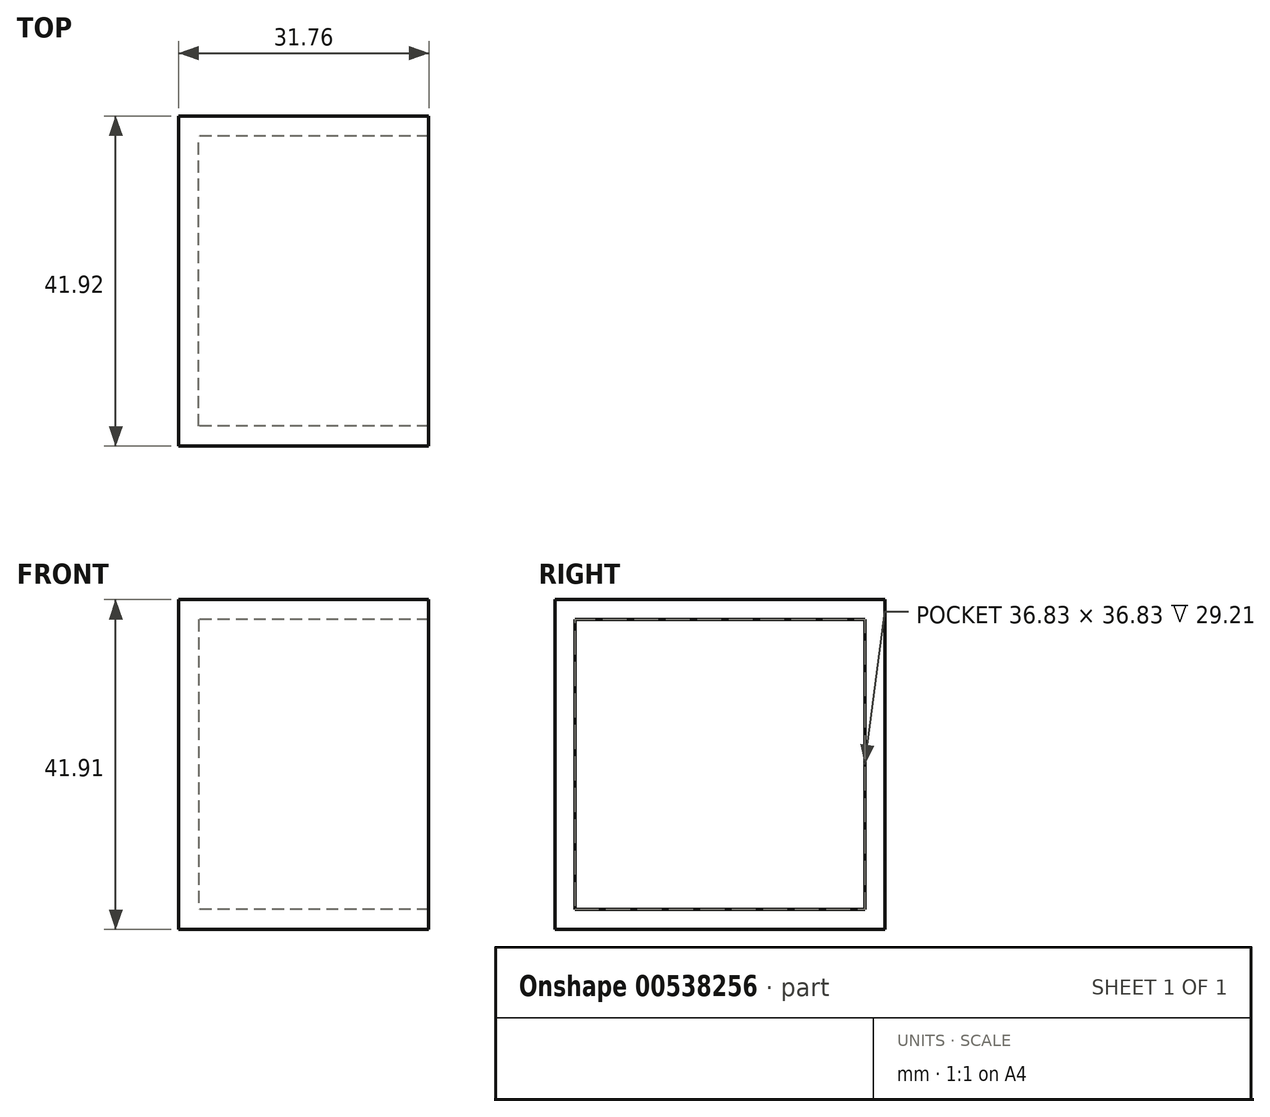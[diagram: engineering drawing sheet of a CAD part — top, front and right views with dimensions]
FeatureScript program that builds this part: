
annotation { "Feature Type Name" : "Feature", "Feature Type Description" : "" }
export const myFeature = defineFeature(function(context is Context, id is Id, definition is map)
    precondition{}
    {
        {
            var Q0;
            Q0=qCreatedBy(makeId("Top.planeOp"),FACE);
            var sketch = newSketch(context, id + "F0", { "sketchPlane" : qUnion([Q0])});
            skPoint(sketch, "E0.middle", {"position": v(0, 0) * mm});
            skLineSegment(sketch, "E1.bottom", {"start": v(14.6, -20.95) * mm, "end": v(-14.6, -20.96) * mm});
            skLineSegment(sketch, "E1.top", {"start": v(14.6, 20.96) * mm, "end": v(-14.6, 20.95) * mm});
            skLineSegment(sketch, "E2.bottom", {"start": v(15.88, -20.96) * mm, "end": v(-15.88, -20.96) * mm});
            skLineSegment(sketch, "E2.top", {"start": v(15.88, 20.96) * mm, "end": v(-15.88, 20.95) * mm});
            skLineSegment(sketch, "E2.left", {"start": v(15.88, -20.95) * mm, "end": v(15.88, 20.96) * mm});
            skLineSegment(sketch, "E2.right", {"start": v(-15.88, -20.96) * mm, "end": v(-15.88, 20.95) * mm});
            skSolve(sketch);
        }
        {
            var Q0;
            {var subQ0=sQuery(id+"F0.wireOp",EDGE,"E2.left");Q0=makeQuery(id+"F0.imprint","IMPRINT",FACE,{"disambiguationData":[TD([[makeQuery(id+"F0.imprint","IMPRINT",EDGE,{"derivedFrom":subQ0}),1.0]])]});}
            extrude(context, id + "F1", {"entities" : qUnion([Q0]), "depth" : 41.9 * mm, "offsetDistance" : 25.4 * mm});
        }
        {
            var Q0;
            Q0=makeQuery(id+"F1.opExtrude","SWEPT_FACE",FACE,{"disambiguationData":[OSD([sQuery(id+"F0.wireOp",EDGE,"E2.left")])]});
            shell(context, id + "F2", {"entities" : qUnion([Q0]), "thickness" : 2.54 * mm});
        }
    });
